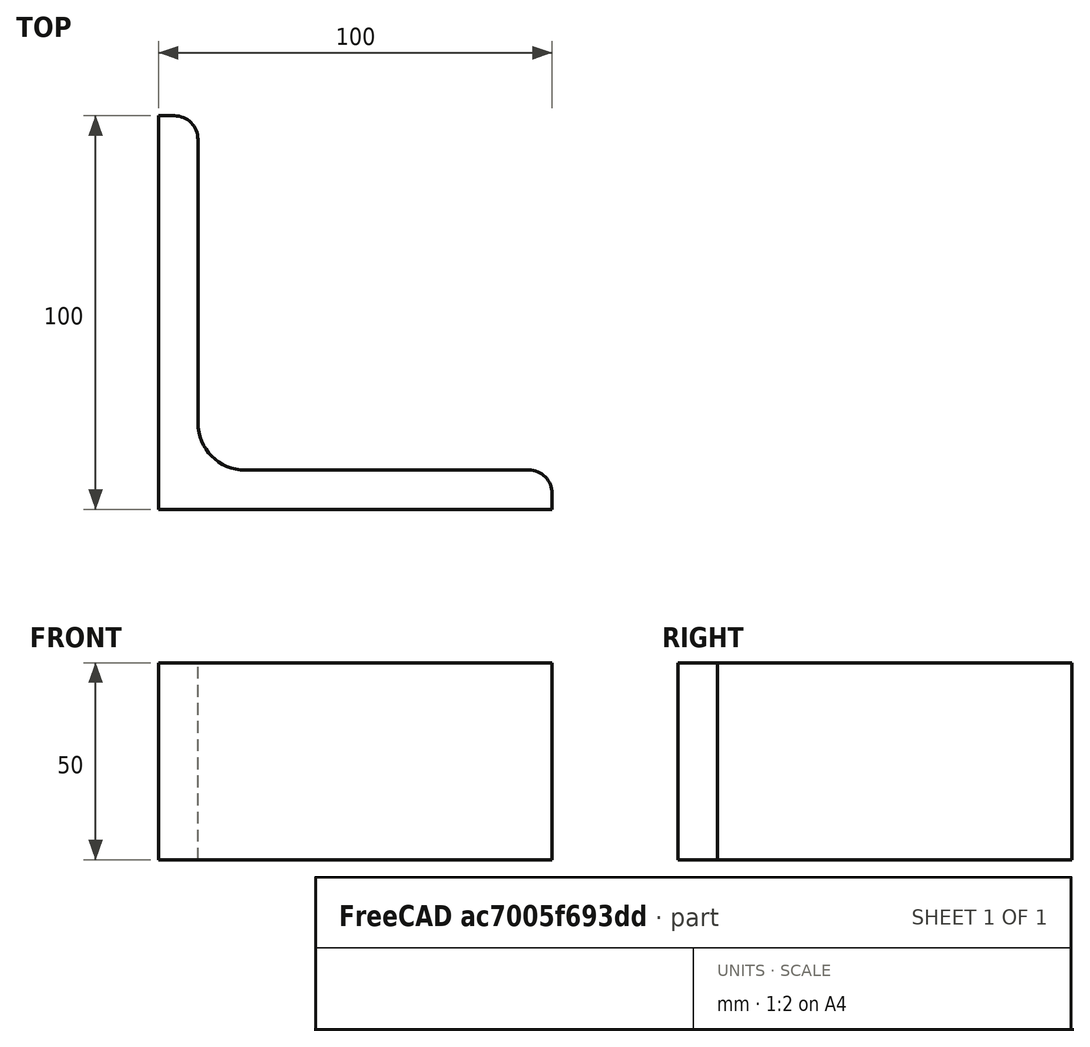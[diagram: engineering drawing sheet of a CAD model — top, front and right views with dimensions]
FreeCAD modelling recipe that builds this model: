
FCSTD DOCUMENT  (FreeCAD 0.15R4671 (Git))
Label: Angle Bar L100x100x10 EN10056 S235JR
License: All rights reserved
LicenseURL: http://en.wikipedia.org/wiki/All_rights_reserved
objects: Sketcher::SketchObject×1, Part::Extrusion×1
note: 2 computed .brp shape members not serialized (recipe doc carries the construction recipe); baked Part::Feature solids carry a one-line shape summary decoded from their .brp

FEATURE [Sketcher::SketchObject] Sketch
  sketch-geometry (9):
    g0: LineSegment StartX=0 StartY=0 StartZ=0 EndX=100 EndY=0 EndZ=0
    g1: LineSegment StartX=100 StartY=0 StartZ=0 EndX=100 EndY=4 EndZ=0
    g2: LineSegment StartX=94 StartY=10 StartZ=0 EndX=22 EndY=10 EndZ=0
    g3: LineSegment StartX=0 StartY=0 StartZ=0 EndX=0 EndY=100 EndZ=0
    g4: LineSegment StartX=0 StartY=100 StartZ=0 EndX=4 EndY=100 EndZ=0
    g5: LineSegment StartX=10 StartY=94 StartZ=0 EndX=10 EndY=22 EndZ=0
    g6: ArcOfCircle CenterX=22 CenterY=22 CenterZ=0 NormalX=0 NormalY=0 NormalZ=1 Radius=12 StartAngle=3.14159 EndAngle=4.71239
    g7: ArcOfCircle CenterX=4 CenterY=94 CenterZ=0 NormalX=0 NormalY=0 NormalZ=1 Radius=6 StartAngle=0 EndAngle=1.5708
    g8: ArcOfCircle CenterX=94 CenterY=4 CenterZ=0 NormalX=0 NormalY=0 NormalZ=1 Radius=6 StartAngle=0 EndAngle=1.5708
  constraints (23):
    c: Coincident(g0,g-1)
    c: Horizontal(g0)
    c: Coincident(g1,g0)
    c: Vertical(g1)
    c: Horizontal(g2)
    c: Coincident(g3,g-1)
    c: Vertical(g3)
    c: Coincident(g4,g3)
    c: Horizontal(g4)
    c: Vertical(g5)
    c: Tangent(g5,g6) = -1.5708
    c: Tangent(g2,g6) = 1.5708
    c: Tangent(g4,g7) = 1.5708
    c: Tangent(g5,g7) = 1.5708
    c: Tangent(g2,g8) = -1.5708
    c: Tangent(g1,g8) = -1.5708
    c: DistanceX(g0) = 100
    c: DistanceY(g3) = 100
    c: DistanceY(g0,g2) = 10
    c: DistanceX(g3,g5) = 10
    c: Radius(g6) = 12
    c: Radius(g8) = 6
    c: Radius(g7) = 6
FEATURE [Part::Extrusion] Extrude  label="Angle Bar L100x100x10 EN10056 S235JR"
  Base = -> Sketch
  Dir = (0,0,50)
  Solid = true
